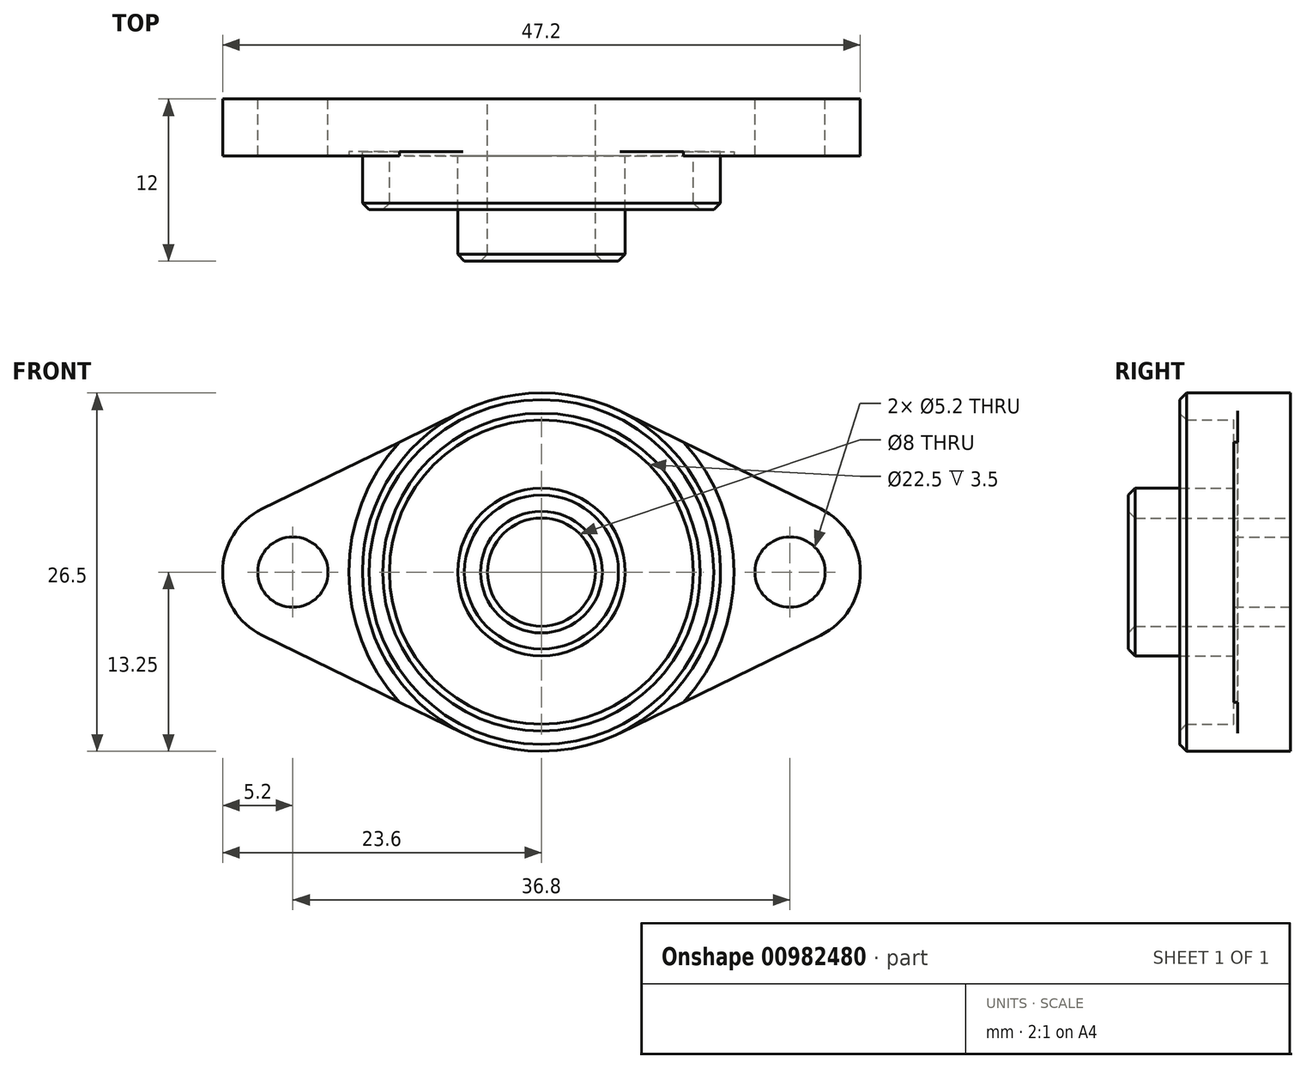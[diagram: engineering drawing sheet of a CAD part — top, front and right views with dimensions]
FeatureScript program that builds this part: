
annotation { "Feature Type Name" : "Feature", "Feature Type Description" : "" }
export const myFeature = defineFeature(function(context is Context, id is Id, definition is map)
    precondition{}
    {
        {
            var Q0;
            Q0=qCreatedBy(makeId("Front.planeOp"),FACE);
            var sketch = newSketch(context, id + "F0", { "sketchPlane" : qUnion([Q0])});
            skCircle(sketch, "E0", {"center": v(0, 0) * mm, "radius": 4 * mm});
            skCircle(sketch, "E1", {"center": v(0, 0) * mm, "radius": 13.25 * mm});
            skLineSegment(sketch, "E2", {"start": v(-18.4, 0) * mm, "end": v(0, 0) * mm, "construction": true});
            skLineSegment(sketch, "E3", {"start": v(0, 0) * mm, "end": v(18.4, 0) * mm, "construction": true});
            skCircle(sketch, "E4", {"center": v(-18.4, 0) * mm, "radius": 2.6 * mm});
            skCircle(sketch, "E5", {"center": v(18.4, 0) * mm, "radius": 2.6 * mm});
            skLineSegment(sketch, "E6", {"start": v(-5.8, 11.91) * mm, "end": v(-20.68, 4.68) * mm});
            skLineSegment(sketch, "E7", {"start": v(-5.8, -11.91) * mm, "end": v(-20.68, -4.68) * mm});
            skArc(sketch, "E8", {"start": v(-20.68, 4.68) * mm, "mid": v(-23.6, 0) * mm, "end": v(-20.68, -4.68) * mm});
            skArc(sketch, "E9", {"start": v(20.68, 4.68) * mm, "mid": v(23.6, 0) * mm, "end": v(20.68, -4.68) * mm});
            skLineSegment(sketch, "E10", {"start": v(20.68, 4.68) * mm, "end": v(5.8, 11.91) * mm});
            skLineSegment(sketch, "E11", {"start": v(5.8, -11.91) * mm, "end": v(20.68, -4.68) * mm});
            skPoint(sketch, "E12", {"position": v(-13.25, 0) * mm});
            skPoint(sketch, "E13", {"position": v(13.25, 0) * mm});
            skPoint(sketch, "E14", {"position": v(-15.8, 0) * mm});
            skPoint(sketch, "E15", {"position": v(15.8, 0) * mm});
            skSolve(sketch);
        }
        {
            var Q0;
            Q0=makeQuery(id+"F0.imprint","IMPRINT",FACE,{"disambiguationData":[TD([[makeQuery(id+"F0.imprint","IMPRINT",EDGE,{"derivedFrom":sQuery(id+"F0.wireOp",EDGE,"E4")}),-1.0]])]});
            var Q1;
            Q1=makeQuery(id+"F0.imprint","IMPRINT",FACE,{"disambiguationData":[TD([[makeQuery(id+"F0.imprint","IMPRINT",EDGE,{"derivedFrom":sQuery(id+"F0.wireOp",EDGE,"E0")}),-1.0]])]});
            var Q2;
            Q2=makeQuery(id+"F0.imprint","IMPRINT",FACE,{"disambiguationData":[TD([[makeQuery(id+"F0.imprint","IMPRINT",EDGE,{"derivedFrom":sQuery(id+"F0.wireOp",EDGE,"E5")}),-1.0]])]});
            extrude(context, id + "F1", {"entities" : qUnion([Q0, Q1, Q2]), "depth" : 4.2 * mm, "offsetDistance" : 25 * mm});
        }
        {
            var Q0;
            Q0=makeQuery(id+"F1.opExtrude","CAP_FACE",FACE,{"disambiguationData":[OSD([sQuery(id+"F0.wireOp",EDGE,"E0"),sQuery(id+"F0.wireOp",EDGE,"E1"),sQuery(id+"F0.wireOp",EDGE,"E4"),sQuery(id+"F0.wireOp",EDGE,"E5"),sQuery(id+"F0.wireOp",EDGE,"E6"),sQuery(id+"F0.wireOp",EDGE,"E7"),sQuery(id+"F0.wireOp",EDGE,"E8"),sQuery(id+"F0.wireOp",EDGE,"E9"),sQuery(id+"F0.wireOp",EDGE,"E10"),sQuery(id+"F0.wireOp",EDGE,"E11")])],"isStart":false});
            var sketch = newSketch(context, id + "F2", { "sketchPlane" : qUnion([Q0])});
            skCircle(sketch, "E16.0", {"center": v(0, 0) * mm, "radius": 13.25 * mm});
            skCircle(sketch, "E17", {"center": v(0, 0) * mm, "radius": 14.25 * mm});
            skSolve(sketch);
        }
        {
            var Q0;
            Q0=qSketchRegion(id+"F2",true);
            extrude(context, id + "F3", {"entities" : qUnion([Q0]), "operationType" : NewBodyOperationType.REMOVE, "oppositeDirection" : true, "depth" : 0.3 * mm, "offsetDistance" : 25 * mm});
        }
        {
            var Q0;
            {var subQ0=sQuery(id+"F0.wireOp",EDGE,"E0");var subQ1=sQuery(id+"F0.wireOp",EDGE,"E6");var subQ2=sQuery(id+"F0.wireOp",EDGE,"E1");var subQ3=sQuery(id+"F0.wireOp",EDGE,"E10");var subQ4=sQuery(id+"F0.wireOp",EDGE,"E7");var subQ5=sQuery(id+"F0.wireOp",EDGE,"E11");Q0=makeQuery(id+"F3.boolean.opBoolean","SPLIT",FACE,{"disambiguationData":[TD([makeQuery(id+"F1.opExtrude","SWEPT_FACE",FACE,{"disambiguationData":[OSD([subQ0])]})])],"derivedFrom":makeQuery(id+"F1.opExtrude","CAP_FACE",FACE,{"disambiguationData":[OSD([subQ0,subQ2,sQuery(id+"F0.wireOp",EDGE,"E4"),sQuery(id+"F0.wireOp",EDGE,"E5"),subQ1,subQ4,sQuery(id+"F0.wireOp",EDGE,"E8"),sQuery(id+"F0.wireOp",EDGE,"E9"),subQ3,subQ5])],"isStart":false})});}
            var sketch = newSketch(context, id + "F4", { "sketchPlane" : qUnion([Q0])});
            skCircle(sketch, "E18.0", {"center": v(0, 0) * mm, "radius": 4 * mm});
            skCircle(sketch, "E19", {"center": v(0, 0) * mm, "radius": 6.2 * mm});
            skCircle(sketch, "E20.0", {"center": v(0, 0) * mm, "radius": 13.25 * mm});
            skCircle(sketch, "E21", {"center": v(0, 0) * mm, "radius": 11.25 * mm});
            skSolve(sketch);
        }
        {
            var Q0;
            Q0=makeQuery(id+"F4.imprint","IMPRINT",FACE,{"disambiguationData":[TD([[makeQuery(id+"F4.imprint","IMPRINT",EDGE,{"derivedFrom":sQuery(id+"F4.wireOp",EDGE,"E18.0")}),-1.0]])]});
            extrude(context, id + "F5", {"entities" : qUnion([Q0]), "operationType" : NewBodyOperationType.ADD, "depth" : (12 - 4.2) * mm, "offsetDistance" : 25 * mm});
        }
        {
            var Q0;
            Q0=makeQuery(id+"F4.imprint","IMPRINT",FACE,{"disambiguationData":[TD([[makeQuery(id+"F4.imprint","IMPRINT",EDGE,{"derivedFrom":sQuery(id+"F4.wireOp",EDGE,"E20.0")}),1.0]])]});
            extrude(context, id + "F6", {"entities" : qUnion([Q0]), "operationType" : NewBodyOperationType.ADD, "depth" : 4 * mm, "offsetDistance" : 25 * mm});
        }
        {
            var Q0;
            Q0=makeQuery(id+"F5.opExtrude","CAP_EDGE",EDGE,{"disambiguationData":[OSD([sQuery(id+"F4.wireOp",EDGE,"E18.0")])],"isStart":false});
            var Q1;
            Q1=makeQuery(id+"F5.opExtrude","CAP_EDGE",EDGE,{"disambiguationData":[OSD([sQuery(id+"F4.wireOp",EDGE,"E19")])],"isStart":false});
            var Q2;
            Q2=makeQuery(id+"F6.opExtrude","CAP_EDGE",EDGE,{"disambiguationData":[OSD([sQuery(id+"F4.wireOp",EDGE,"E21")])],"isStart":false});
            var Q3;
            Q3=makeQuery(id+"F6.opExtrude","CAP_EDGE",EDGE,{"disambiguationData":[OSD([sQuery(id+"F4.wireOp",EDGE,"E20.0")])],"isStart":false});
            chamfer(context, id + "F7", {"entities" : qUnion([Q0, Q1, Q2, Q3]), "width" : 0.5 * mm, "tangentPropagation" : true});
        }
    });
